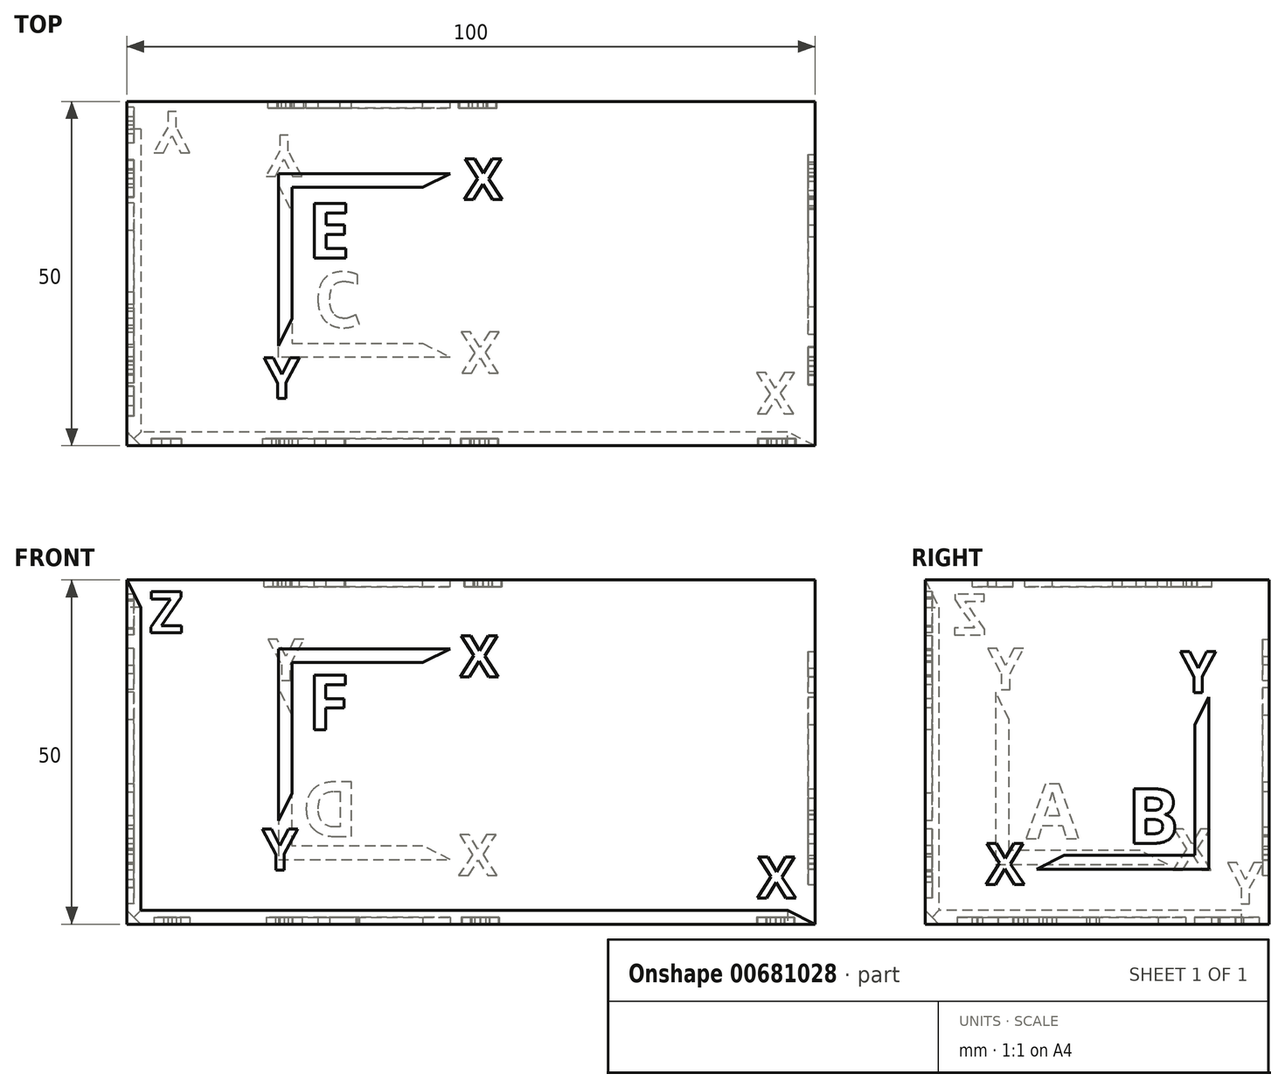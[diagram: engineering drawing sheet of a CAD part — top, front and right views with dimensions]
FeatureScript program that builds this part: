
annotation { "Feature Type Name" : "Feature", "Feature Type Description" : "" }
export const myFeature = defineFeature(function(context is Context, id is Id, definition is map)
    precondition{}
    {
        {
            var Q0;
            Q0=qCreatedBy(makeId("Top.planeOp"),FACE);
            var sketch = newSketch(context, id + "F0", { "sketchPlane" : qUnion([Q0])});
            skLineSegment(sketch, "E0.bottom", {"start": v(0, 0) * mm, "end": v(100, 0) * mm});
            skLineSegment(sketch, "E0.top", {"start": v(0, 50) * mm, "end": v(100, 50) * mm});
            skLineSegment(sketch, "E0.left", {"start": v(0, 50) * mm, "end": v(0, 0) * mm});
            skLineSegment(sketch, "E0.right", {"start": v(100, 50) * mm, "end": v(100, 0) * mm});
            skLineSegment(sketch, "E1", {"start": v(0, 0) * mm, "end": v(96, 0) * mm, "construction": true});
            skSolve(sketch);
        }
        {
            var Q0;
            Q0 = qSketchRegion(id + "F0", true);
            extrude(context, id + "F1", {"entities" : qUnion([Q0]), "depth" : 50 * mm, "offsetDistance" : 25 * mm});
        }
        {
            var Q0;
            Q0=makeQuery(id+"F1.opExtrude","SWEPT_FACE",FACE,{"disambiguationData":[OSD([sQuery(id+"F0.wireOp",EDGE,"E0.left")])]});
            var sketch = newSketch(context, id + "F2", { "sketchPlane" : qUnion([Q0])});
            skLineSegment(sketch, "E2", {"start": v(0, 2) * mm, "end": v(-2, 0) * mm});
            skLineSegment(sketch, "E3", {"start": v(-2, 0) * mm, "end": v(0, 0) * mm});
            skLineSegment(sketch, "E4", {"start": v(0, 0) * mm, "end": v(0, 2) * mm});
            skSolve(sketch);
        }
        {
            var Q0;
            Q0 = qSketchRegion(id + "F2", true);
            var Q1;
            Q1=makeQuery(id+"F1.opExtrude","SWEPT_FACE",FACE,{"disambiguationData":[OSD([sQuery(id+"F0.wireOp",EDGE,"E0.right")])]});
            extrude(context, id + "F3", {"entities" : qUnion([Q0]), "operationType" : NewBodyOperationType.REMOVE, "endBound" : BoundingType.UP_TO_SURFACE, "oppositeDirection" : true, "depth" : 25 * mm, "endBoundEntityFace" : qUnion([Q1]), "hasOffset" : true, "offsetDistance" : 4 * mm});
        }
        {
            var Q0;
            Q0=makeQuery(id+"F3.boolean.opBoolean","COPY",VERTEX,{"derivedFrom":makeQuery(id+"F3.opExtrude","CAP_VERTEX",VERTEX,{"disambiguationData":[OSD([sQuery(id+"F0.wireOp",EDGE,"E0.bottom"),sQuery(id+"F0.wireOp",EDGE,"E0.left"),sQuery(id+"F0.wireOp",EDGE,"E0.right"),sQuery(id+"F2.wireOp",EDGE,"E2"),sQuery(id+"F2.wireOp",EDGE,"E4")])],"isStart":false})});
            var Q1;
            Q1=makeQuery(id+"F3.boolean.opBoolean","COPY",VERTEX,{"derivedFrom":makeQuery(id+"F3.opExtrude","CAP_VERTEX",VERTEX,{"disambiguationData":[OSD([sQuery(id+"F0.wireOp",EDGE,"E0.left"),sQuery(id+"F0.wireOp",EDGE,"E0.right"),sQuery(id+"F2.wireOp",EDGE,"E2"),sQuery(id+"F2.wireOp",EDGE,"E3")])],"isStart":false})});
            var Q2;
            Q2=makeQuery(id+"F1.opExtrude","CAP_VERTEX",VERTEX,{"disambiguationData":[OSD([sQuery(id+"F0.wireOp",EDGE,"E0.bottom"),sQuery(id+"F0.wireOp",EDGE,"E0.right")])],"isStart":true});
            cPlane(context, id + "F4", {"entities" : qUnion([Q0, Q1, Q2]), "cplaneType" : CPlaneType.THREE_POINT, "offset" : 0 * mm, "width" : 150 * mm, "height" : 150 * mm});
        }
        {
            var Q0;
            Q0=qCreatedBy(id+"F4.planeOp",FACE);
            var sketch = newSketch(context, id + "F5", { "sketchPlane" : qUnion([Q0])});
            skLineSegment(sketch, "E5", {"start": v(-90.04, 1.41) * mm, "end": v(-94.28, 0) * mm});
            skLineSegment(sketch, "E6", {"start": v(-94.28, 0) * mm, "end": v(-90.04, -1.41) * mm});
            skLineSegment(sketch, "E7", {"start": v(-90.04, -1.41) * mm, "end": v(-90.04, 1.41) * mm});
            skSolve(sketch);
        }
        {
            var Q0;
            Q0 = qSketchRegion(id + "F5", true);
            extrude(context, id + "F6", {"entities" : qUnion([Q0]), "operationType" : NewBodyOperationType.REMOVE, "oppositeDirection" : true, "depth" : 25 * mm, "offsetDistance" : 25 * mm});
        }
        {
            var Q0;
            Q0=makeQuery(id+"F1.opExtrude","SWEPT_FACE",FACE,{"disambiguationData":[OSD([sQuery(id+"F0.wireOp",EDGE,"E0.bottom")])]});
            var sketch = newSketch(context, id + "F7", { "sketchPlane" : qUnion([Q0])});
            skLineSegment(sketch, "E8", {"start": v(0, 0) * mm, "end": v(0, 2) * mm});
            skLineSegment(sketch, "E9", {"start": v(0, 2) * mm, "end": v(2, 0) * mm});
            skLineSegment(sketch, "E10", {"start": v(2, 0) * mm, "end": v(0, 0) * mm});
            skLineSegment(sketch, "E11", {"start": v(0, 0) * mm, "end": v(2, 0) * mm});
            skSolve(sketch);
        }
        {
            var Q0;
            Q0=makeQuery(id+"F7.imprint","IMPRINT",FACE,{"disambiguationData":[TD([[makeQuery(id+"F7.imprint","IMPRINT",EDGE,{"derivedFrom":sQuery(id+"F7.wireOp",EDGE,"E9")}),-1.0]])]});
            var Q1;
            Q1=sQuery(id+"F7.wireOp",EDGE,"E11");
            var Q2;
            Q2=sQuery(id+"F7.wireOp",EDGE,"E10");
            extrude(context, id + "F8", {"entities" : qUnion([Q0]), "operationType" : NewBodyOperationType.REMOVE, "surfaceEntities" : qUnion([Q1, Q2]), "oppositeDirection" : true, "depth" : 46 * mm, "offsetDistance" : 25 * mm});
        }
        {
            var Q0;
            Q0=makeQuery(id+"F1.opExtrude","CAP_FACE",FACE,{"disambiguationData":[OSD([sQuery(id+"F0.wireOp",EDGE,"E0.bottom"),sQuery(id+"F0.wireOp",EDGE,"E0.top"),sQuery(id+"F0.wireOp",EDGE,"E0.left"),sQuery(id+"F0.wireOp",EDGE,"E0.right")])],"isStart":true});
            var sketch = newSketch(context, id + "F9", { "sketchPlane" : qUnion([Q0])});
            skLineSegment(sketch, "E12", {"start": v(2, 0) * mm, "end": v(0, 0) * mm});
            skLineSegment(sketch, "E13", {"start": v(0, 0) * mm, "end": v(0, -2) * mm});
            skLineSegment(sketch, "E14", {"start": v(2, 0) * mm, "end": v(0, -2) * mm});
            skSolve(sketch);
        }
        {
            var Q0;
            Q0 = qSketchRegion(id + "F9", true);
            extrude(context, id + "F10", {"entities" : qUnion([Q0]), "operationType" : NewBodyOperationType.REMOVE, "oppositeDirection" : true, "depth" : 46 * mm, "offsetDistance" : 25 * mm});
        }
        {
            var Q0;
            Q0=makeQuery(id+"F1.opExtrude","CAP_VERTEX",VERTEX,{"disambiguationData":[OSD([sQuery(id+"F0.wireOp",EDGE,"E0.bottom"),sQuery(id+"F0.wireOp",EDGE,"E0.left")])],"isStart":false});
            var Q1;
            Q1=makeQuery(id+"F10.boolean.opBoolean","COPY",VERTEX,{"derivedFrom":makeQuery(id+"F10.opExtrude","CAP_VERTEX",VERTEX,{"disambiguationData":[OSD([sQuery(id+"F9.wireOp",EDGE,"E13"),sQuery(id+"F9.wireOp",EDGE,"E14")])],"isStart":false})});
            var Q2;
            Q2=makeQuery(id+"F10.boolean.opBoolean","COPY",VERTEX,{"derivedFrom":makeQuery(id+"F10.opExtrude","CAP_VERTEX",VERTEX,{"disambiguationData":[OSD([sQuery(id+"F9.wireOp",EDGE,"E12"),sQuery(id+"F9.wireOp",EDGE,"E14")])],"isStart":false})});
            cPlane(context, id + "F11", {"entities" : qUnion([Q0, Q1, Q2]), "cplaneType" : CPlaneType.THREE_POINT, "offset" : 25 * mm, "width" : 150 * mm, "height" : 150 * mm});
        }
        {
            var Q0;
            Q0=qCreatedBy(id+"F11.planeOp",FACE);
            var sketch = newSketch(context, id + "F12", { "sketchPlane" : qUnion([Q0])});
            skLineSegment(sketch, "E15", {"start": v(14.9, 44.72) * mm, "end": v(14.9, 40.25) * mm});
            skLineSegment(sketch, "E16", {"start": v(14.9, 40.25) * mm, "end": v(12.22, 41.14) * mm});
            skLineSegment(sketch, "E17", {"start": v(12.22, 41.14) * mm, "end": v(14.9, 44.72) * mm});
            skSolve(sketch);
        }
        {
            var Q0;
            Q0 = qSketchRegion(id + "F12", true);
            extrude(context, id + "F13", {"entities" : qUnion([Q0]), "operationType" : NewBodyOperationType.REMOVE, "oppositeDirection" : true, "depth" : 25 * mm, "offsetDistance" : 25 * mm});
        }
        {
            var Q0;
            Q0=makeQuery(id+"F8.boolean.opBoolean","COPY",VERTEX,{"derivedFrom":makeQuery(id+"F8.opExtrude","CAP_VERTEX",VERTEX,{"disambiguationData":[OSD([sQuery(id+"F0.wireOp",EDGE,"E0.bottom"),sQuery(id+"F0.wireOp",EDGE,"E0.left"),sQuery(id+"F2.wireOp",EDGE,"E2"),sQuery(id+"F2.wireOp",EDGE,"E4"),sQuery(id+"F7.wireOp",EDGE,"E9"),sQuery(id+"F7.wireOp",EDGE,"E8")])],"isStart":false})});
            var Q1;
            Q1=makeQuery(id+"F8.boolean.opBoolean","COPY",VERTEX,{"derivedFrom":makeQuery(id+"F8.opExtrude","CAP_VERTEX",VERTEX,{"disambiguationData":[OSD([sQuery(id+"F7.wireOp",EDGE,"E9"),sQuery(id+"F7.wireOp",EDGE,"E11")])],"isStart":false})});
            var Q2;
            Q2=makeQuery(id+"F1.opExtrude","CAP_VERTEX",VERTEX,{"disambiguationData":[OSD([sQuery(id+"F0.wireOp",EDGE,"E0.top"),sQuery(id+"F0.wireOp",EDGE,"E0.left")])],"isStart":true});
            cPlane(context, id + "F14", {"entities" : qUnion([Q0, Q1, Q2]), "cplaneType" : CPlaneType.THREE_POINT, "offset" : 25 * mm, "width" : 150 * mm, "height" : 150 * mm});
        }
        {
            var Q0;
            Q0=qCreatedBy(id+"F14.planeOp",FACE);
            var sketch = newSketch(context, id + "F15", { "sketchPlane" : qUnion([Q0])});
            skLineSegment(sketch, "E18", {"start": v(-14.9, -40.25) * mm, "end": v(-14.9, -44.72) * mm});
            skLineSegment(sketch, "E19", {"start": v(-14.9, -44.72) * mm, "end": v(-12.22, -41.14) * mm});
            skLineSegment(sketch, "E20", {"start": v(-14.9, -40.25) * mm, "end": v(-12.22, -41.14) * mm});
            skSolve(sketch);
        }
        {
            var Q0;
            Q0 = qSketchRegion(id + "F15", true);
            extrude(context, id + "F16", {"entities" : qUnion([Q0]), "operationType" : NewBodyOperationType.REMOVE, "depth" : 25 * mm, "offsetDistance" : 25 * mm});
        }
        {
            var Q0;
            Q0=makeQuery(id+"F1.opExtrude","SWEPT_FACE",FACE,{"disambiguationData":[OSD([sQuery(id+"F0.wireOp",EDGE,"E0.bottom")])]});
            var sketch = newSketch(context, id + "F17", { "sketchPlane" : qUnion([Q0])});
            skLineSegment(sketch, "E21", {"start": v(22, 40) * mm, "end": v(22, 15) * mm});
            skLineSegment(sketch, "E22", {"start": v(22, 15) * mm, "end": v(24, 19) * mm});
            skLineSegment(sketch, "E23", {"start": v(24, 19) * mm, "end": v(24, 38) * mm});
            skLineSegment(sketch, "E24", {"start": v(24, 38) * mm, "end": v(43, 38) * mm});
            skLineSegment(sketch, "E25", {"start": v(43, 38) * mm, "end": v(47, 40) * mm});
            skLineSegment(sketch, "E26", {"start": v(47, 40) * mm, "end": v(22, 40) * mm});
            skText(sketch, "E27", { "text": "Y", "fontName": "OpenSans-Bold.ttf"});
            skText(sketch, "E28", { "text": "X", "fontName": "OpenSans-Bold.ttf"});
            skText(sketch, "E29", { "text": "F", "fontName": "OpenSans-Bold.ttf"});
            skText(sketch, "E30", { "text": "Z", "fontName": "OpenSans-Bold.ttf"});
            skText(sketch, "E31", { "text": "X", "fontName": "OpenSans-Bold.ttf"});
            const initialGuessF17  = {"E27": [0.01965, 0.00788, 1, 0, 0.006], "E28": [0.04843, 0.03594, 1, 0, 0.006], "E29": [0.02621, 0.02825, 1, 0, 0.008], "E30": [0.0033, 0.04233, 1, 0, 0.006], "E31": [0.09163, 0.00381, 1, 0, 0.006]};
            skSetInitialGuess(sketch, initialGuessF17);
            skSolve(sketch);
        }
        {
            var Q0;
            Q0 = qSketchRegion(id + "F17", true);
            var Q1;
            Q1 = qConstructionFilter(qBodyType(qCreatedBy(id + "F17" ,EDGE), BodyType.WIRE), ConstructionObject.NO);
            extrude(context, id + "F18", {"entities" : qUnion([Q0]), "operationType" : NewBodyOperationType.REMOVE, "surfaceEntities" : qUnion([Q1]), "oppositeDirection" : true, "depth" : 1 * mm, "offsetDistance" : 25 * mm});
        }
        {
            var Q0;
            Q0=makeQuery(id+"F1.opExtrude","CAP_FACE",FACE,{"disambiguationData":[OSD([sQuery(id+"F0.wireOp",EDGE,"E0.bottom"),sQuery(id+"F0.wireOp",EDGE,"E0.top"),sQuery(id+"F0.wireOp",EDGE,"E0.left"),sQuery(id+"F0.wireOp",EDGE,"E0.right")])],"isStart":true});
            var sketch = newSketch(context, id + "F19", { "sketchPlane" : qUnion([Q0])});
            skLineSegment(sketch, "E32", {"start": v(22, -12.86) * mm, "end": v(22, -37.86) * mm});
            skLineSegment(sketch, "E33", {"start": v(22, -37.86) * mm, "end": v(24, -33.86) * mm});
            skLineSegment(sketch, "E34", {"start": v(24, -33.86) * mm, "end": v(24, -14.86) * mm});
            skLineSegment(sketch, "E35", {"start": v(24, -14.86) * mm, "end": v(43, -14.86) * mm});
            skLineSegment(sketch, "E36", {"start": v(43, -14.86) * mm, "end": v(47, -12.86) * mm});
            skLineSegment(sketch, "E37", {"start": v(47, -12.86) * mm, "end": v(22, -12.86) * mm});
            skText(sketch, "E38", { "text": "Y", "fontName": "OpenSans-Bold.ttf"});
            skText(sketch, "E39", { "text": "X", "fontName": "OpenSans-Bold.ttf"});
            skText(sketch, "E40", { "text": "X", "fontName": "OpenSans-Bold.ttf"});
            skText(sketch, "E41", { "text": "C", "fontName": "OpenSans-Bold.ttf"});
            skText(sketch, "E42", { "text": "Y", "fontName": "OpenSans-Bold.ttf"});
            const initialGuessF19  = {"E38": [0.02023, -0.0451, 1, 0, 0.006], "E39": [0.04856, -0.01652, 1, 0, 0.006], "E40": [0.09147, -0.0106, 1, 0, 0.006], "E41": [0.02711, -0.02516, 1, 0, 0.008], "E42": [0.00396, -0.04853, 1, 0, 0.006]};
            skSetInitialGuess(sketch, initialGuessF19);
            skSolve(sketch);
        }
        {
            var Q0;
            Q0 = qSketchRegion(id + "F19", true);
            extrude(context, id + "F20", {"entities" : qUnion([Q0]), "operationType" : NewBodyOperationType.REMOVE, "oppositeDirection" : true, "depth" : 1 * mm, "offsetDistance" : 25 * mm});
        }
        {
            var Q0;
            Q0=makeQuery(id+"F1.opExtrude","CAP_FACE",FACE,{"disambiguationData":[OSD([sQuery(id+"F0.wireOp",EDGE,"E0.bottom"),sQuery(id+"F0.wireOp",EDGE,"E0.top"),sQuery(id+"F0.wireOp",EDGE,"E0.left"),sQuery(id+"F0.wireOp",EDGE,"E0.right")])],"isStart":false});
            var sketch = newSketch(context, id + "F21", { "sketchPlane" : qUnion([Q0])});
            skLineSegment(sketch, "E43", {"start": v(22, 39.51) * mm, "end": v(22, 14.51) * mm});
            skLineSegment(sketch, "E44", {"start": v(22, 14.51) * mm, "end": v(24, 18.51) * mm});
            skLineSegment(sketch, "E45", {"start": v(24, 18.51) * mm, "end": v(24, 37.51) * mm});
            skLineSegment(sketch, "E46", {"start": v(24, 37.51) * mm, "end": v(43, 37.51) * mm});
            skLineSegment(sketch, "E47", {"start": v(43, 37.51) * mm, "end": v(47, 39.51) * mm});
            skLineSegment(sketch, "E48", {"start": v(47, 39.51) * mm, "end": v(22, 39.51) * mm});
            skText(sketch, "E49", { "text": "Y", "fontName": "OpenSans-Bold.ttf"});
            skText(sketch, "E50", { "text": "X", "fontName": "OpenSans-Bold.ttf"});
            skText(sketch, "E51", { "text": "E", "fontName": "OpenSans-Bold.ttf"});
            const initialGuessF21  = {"E49": [0.01991, 0.00684, 1, 0, 0.006], "E50": [0.049, 0.03574, 1, 0, 0.006], "E51": [0.02624, 0.02726, 1, 0, 0.008]};
            skSetInitialGuess(sketch, initialGuessF21);
            skSolve(sketch);
        }
        {
            var Q0;
            Q0 = qSketchRegion(id + "F21", true);
            extrude(context, id + "F22", {"entities" : qUnion([Q0]), "operationType" : NewBodyOperationType.REMOVE, "oppositeDirection" : true, "depth" : 1 * mm, "offsetDistance" : 25 * mm});
        }
        {
            var Q0;
            Q0=makeQuery(id+"F1.opExtrude","SWEPT_FACE",FACE,{"disambiguationData":[OSD([sQuery(id+"F0.wireOp",EDGE,"E0.top")])]});
            var sketch = newSketch(context, id + "F23", { "sketchPlane" : qUnion([Q0])});
            skLineSegment(sketch, "E52", {"start": v(-22, 34.37) * mm, "end": v(-22, 9.37) * mm});
            skLineSegment(sketch, "E53", {"start": v(-22, 9.37) * mm, "end": v(-47, 9.37) * mm});
            skLineSegment(sketch, "E54", {"start": v(-47, 9.37) * mm, "end": v(-43, 11.37) * mm});
            skLineSegment(sketch, "E55", {"start": v(-43, 11.37) * mm, "end": v(-24, 11.37) * mm});
            skLineSegment(sketch, "E56", {"start": v(-24, 11.37) * mm, "end": v(-24, 30.37) * mm});
            skLineSegment(sketch, "E57", {"start": v(-24, 30.37) * mm, "end": v(-22, 34.37) * mm});
            skText(sketch, "E58", { "text": "X", "fontName": "OpenSans-Bold.ttf"});
            skText(sketch, "E59", { "text": "Y", "fontName": "OpenSans-Bold.ttf"});
            skText(sketch, "E60", { "text": "D", "fontName": "OpenSans-Bold.ttf"});
            const initialGuessF23  = {"E58": [-0.05378, 0.00707, 1, 0, 0.006], "E59": [-0.0257, 0.0354, 1, 0, 0.006], "E60": [-0.03364, 0.01273, 1, 0, 0.008]};
            skSetInitialGuess(sketch, initialGuessF23);
            skSolve(sketch);
        }
        {
            var Q0;
            Q0 = qSketchRegion(id + "F23", true);
            extrude(context, id + "F24", {"entities" : qUnion([Q0]), "operationType" : NewBodyOperationType.REMOVE, "oppositeDirection" : true, "depth" : 1 * mm, "offsetDistance" : 25 * mm});
        }
        {
            var Q0;
            Q0=makeQuery(id+"F1.opExtrude","SWEPT_FACE",FACE,{"disambiguationData":[OSD([sQuery(id+"F0.wireOp",EDGE,"E0.left")])]});
            var sketch = newSketch(context, id + "F25", { "sketchPlane" : qUnion([Q0])});
            skLineSegment(sketch, "E61", {"start": v(-10.22, 33.7) * mm, "end": v(-10.22, 8.7) * mm});
            skLineSegment(sketch, "E62", {"start": v(-10.22, 8.7) * mm, "end": v(-35.22, 8.7) * mm});
            skLineSegment(sketch, "E63", {"start": v(-35.22, 8.7) * mm, "end": v(-31.22, 10.7) * mm});
            skLineSegment(sketch, "E64", {"start": v(-31.22, 10.7) * mm, "end": v(-12.22, 10.7) * mm});
            skLineSegment(sketch, "E65", {"start": v(-12.22, 10.7) * mm, "end": v(-12.22, 29.7) * mm});
            skLineSegment(sketch, "E66", {"start": v(-12.22, 29.7) * mm, "end": v(-10.22, 33.7) * mm});
            skText(sketch, "E67", { "text": "X", "fontName": "OpenSans-Bold.ttf"});
            skText(sketch, "E68", { "text": "Y", "fontName": "OpenSans-Bold.ttf"});
            skText(sketch, "E69", { "text": "A", "fontName": "OpenSans-Bold.ttf"});
            skText(sketch, "E70", { "text": "Z", "fontName": "OpenSans-Bold.ttf"});
            skText(sketch, "E71", { "text": "Y", "fontName": "OpenSans-Bold.ttf"});
            skPoint(sketch, "E72", {"position": v(-1, 48) * mm});
            const initialGuessF25  = {"E67": [-0.04156, 0.00788, 1, 0, 0.006], "E68": [-0.01427, 0.03407, 1, 0, 0.006], "E69": [-0.02232, 0.01242, 1, 0, 0.008], "E70": [-0.00886, 0.042, 1, 0, 0.006], "E71": [-0.04913, 0.00298, 1, 0, 0.006]};
            skSetInitialGuess(sketch, initialGuessF25);
            skSolve(sketch);
        }
        {
            var Q0;
            Q0 = qSketchRegion(id + "F25", true);
            extrude(context, id + "F26", {"entities" : qUnion([Q0]), "operationType" : NewBodyOperationType.REMOVE, "oppositeDirection" : true, "depth" : 1 * mm, "offsetDistance" : 25 * mm});
        }
        {
            var Q0;
            Q0=makeQuery(id+"F1.opExtrude","SWEPT_FACE",FACE,{"disambiguationData":[OSD([sQuery(id+"F0.wireOp",EDGE,"E0.right")])]});
            var sketch = newSketch(context, id + "F27", { "sketchPlane" : qUnion([Q0])});
            skLineSegment(sketch, "E73", {"start": v(41.21, 33) * mm, "end": v(41.21, 8) * mm});
            skLineSegment(sketch, "E74", {"start": v(41.21, 8) * mm, "end": v(16.21, 8) * mm});
            skLineSegment(sketch, "E75", {"start": v(16.21, 8) * mm, "end": v(20.21, 10) * mm});
            skLineSegment(sketch, "E76", {"start": v(20.21, 10) * mm, "end": v(39.21, 10) * mm});
            skLineSegment(sketch, "E77", {"start": v(39.21, 10) * mm, "end": v(39.21, 29) * mm});
            skLineSegment(sketch, "E78", {"start": v(39.21, 29) * mm, "end": v(41.21, 33) * mm});
            skText(sketch, "E79", { "text": "X", "fontName": "OpenSans-Bold.ttf"});
            skText(sketch, "E80", { "text": "Y", "fontName": "OpenSans-Bold.ttf"});
            skText(sketch, "E81", { "text": "B", "fontName": "OpenSans-Bold.ttf"});
            const initialGuessF27  = {"E79": [0.00885, 0.00577, 1, 0, 0.006], "E80": [0.03707, 0.03366, 1, 0, 0.006], "E81": [0.02939, 0.01175, 1, 0, 0.008]};
            skSetInitialGuess(sketch, initialGuessF27);
            skSolve(sketch);
        }
        {
            var Q0;
            Q0 = qSketchRegion(id + "F27", true);
            extrude(context, id + "F28", {"entities" : qUnion([Q0]), "operationType" : NewBodyOperationType.REMOVE, "oppositeDirection" : true, "depth" : 1 * mm, "offsetDistance" : 25 * mm});
        }
        {
            var Q0;
            Q0=qCreatedBy(makeId("Top.planeOp"),FACE);
            var sketch = newSketch(context, id + "F29", { "sketchPlane" : qUnion([Q0])});
            skLineSegment(sketch, "E82.bottom", {"start": v(0, 0) * mm, "end": v(100, 0) * mm});
            skLineSegment(sketch, "E82.top", {"start": v(0, 50) * mm, "end": v(100, 50) * mm});
            skLineSegment(sketch, "E82.left", {"start": v(0, 0) * mm, "end": v(0, 50) * mm});
            skLineSegment(sketch, "E82.right", {"start": v(100, 0) * mm, "end": v(100, 50) * mm});
            skSolve(sketch);
        }
        {
            var Q0;
            Q0 = qSketchRegion(id + "F29", true);
            extrude(context, id + "F30", {"entities" : qUnion([Q0]), "depth" : 50 * mm, "offsetDistance" : 25 * mm});
        }
    });
